# Revit family: CWSO-WW-S2 ENScape akustisk signalgiver hvit_Vegg
name_source: partatom
category: Fire Alarm Devices
revit_build: Autodesk Revit 2016 (Build: 20160314_0715(x64)
units: mm (PartAtom-declared; Revit-internal decimal feet)

## family parameters
Always vertical = No
Cut with Voids When Loaded = No
Maintain Annotation Orientation = Yes
OmniClass Number = 23.85.30.21.11.17
OmniClass Title = Other Components
Part Type = Normal
Room Calculation Point = No
Round Connector Dimension = Use Diameter
Shared = No
Work Plane-Based = No

## types (1)
- Signalgiver
    Assembly Code = 5423
    CQ Diameter = 100 mm  [stored 0.328084 ft]
    CQ Length = 77 mm  [stored 0.252625 ft]
    CQ Material = Plastic - White
    Keynote = XN1
    Manufacturer = Honeywell
    NS8360 = 5423_XN1
    Type Comments = -XH

note: [stored X ft] marks values corroborated as IEEE doubles in the binary element streams (Revit-internal decimal feet)

## geometry (parser evidence)
native form markers: Sweep x3
no freeform markers — native parametric forms only
